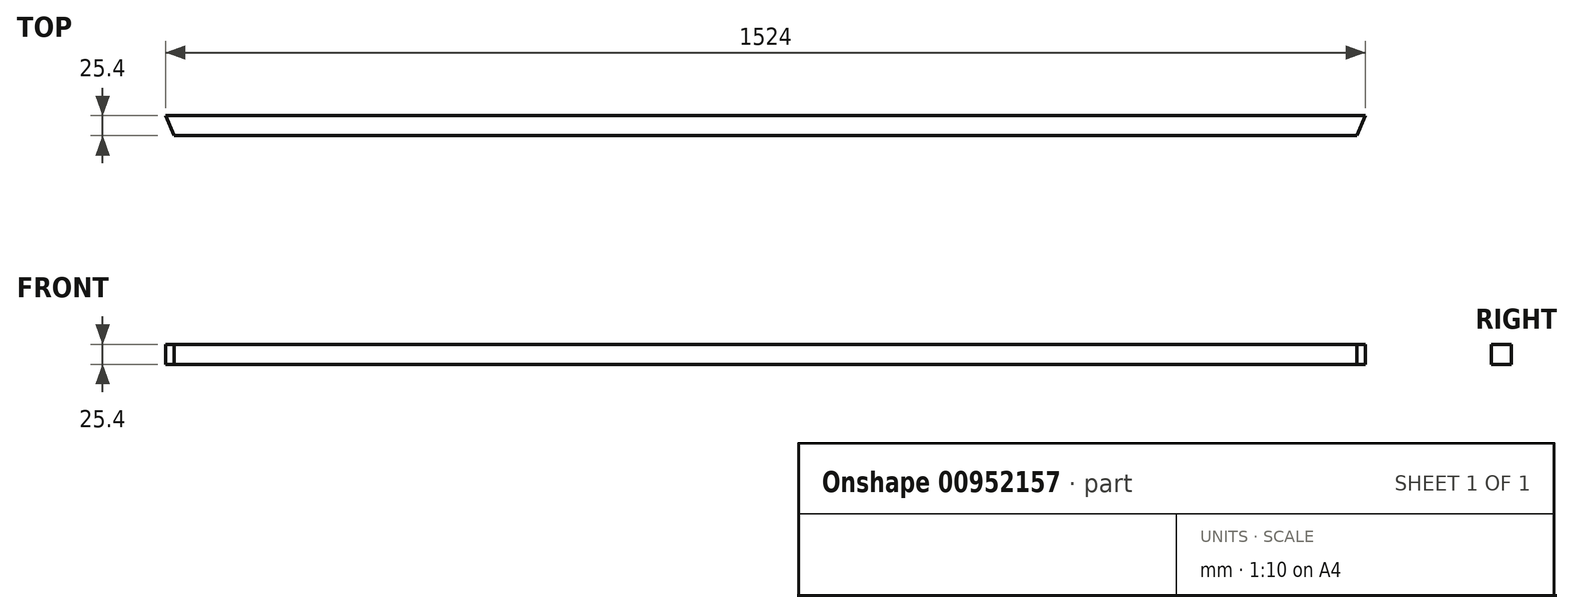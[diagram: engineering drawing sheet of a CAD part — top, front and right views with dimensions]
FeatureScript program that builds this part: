
annotation { "Feature Type Name" : "Feature", "Feature Type Description" : "" }
export const myFeature = defineFeature(function(context is Context, id is Id, definition is map)
    precondition{}
    {
        {
            var Q0;
            Q0=qCreatedBy(makeId("Right.planeOp"),FACE);
            var sketch = newSketch(context, id + "F0", { "sketchPlane" : qUnion([Q0])});
            skLineSegment(sketch, "E0.bottom", {"start": v(12.7, -12.7) * mm, "end": v(-12.7, -12.7) * mm});
            skLineSegment(sketch, "E0.top", {"start": v(12.7, 12.7) * mm, "end": v(-12.7, 12.7) * mm});
            skLineSegment(sketch, "E0.left", {"start": v(12.7, -12.7) * mm, "end": v(12.7, 12.7) * mm});
            skLineSegment(sketch, "E0.right", {"start": v(-12.7, -12.7) * mm, "end": v(-12.7, 12.7) * mm});
            skPoint(sketch, "E0.middle", {"position": v(0, 0) * mm});
            skSolve(sketch);
        }
        {
            var Q0;
            Q0=makeQuery(id+"F0.imprint","IMPRINT",FACE,{"disambiguationData":[TD([[makeQuery(id+"F0.imprint","IMPRINT",EDGE,{"derivedFrom":sQuery(id+"F0.wireOp",EDGE,"E0.bottom")}),-1.0]])]});
            extrude(context, id + "F1", {"entities" : qUnion([Q0]), "endBound" : BoundingType.SYMMETRIC, "depth" : 1524 * mm, "offsetDistance" : 25.4 * mm});
        }
        {
            var Q0;
            Q0=makeQuery(id+"F1.opExtrude","CAP_EDGE",EDGE,{"disambiguationData":[OSD([sQuery(id+"F0.wireOp",EDGE,"E0.right")])],"isStart":false});
            var Q1;
            Q1=makeQuery(id+"F1.opExtrude","CAP_EDGE",EDGE,{"disambiguationData":[OSD([sQuery(id+"F0.wireOp",EDGE,"E0.right")])],"isStart":true});
            chamfer(context, id + "F2", {"entities" : qUnion([Q0, Q1]), "chamferType" : ChamferType.OFFSET_ANGLE, "width" : 25.4 * mm, "oppositeDirection" : true, "angle" : 22.5 * degree, "tangentPropagation" : true});
        }
    });
